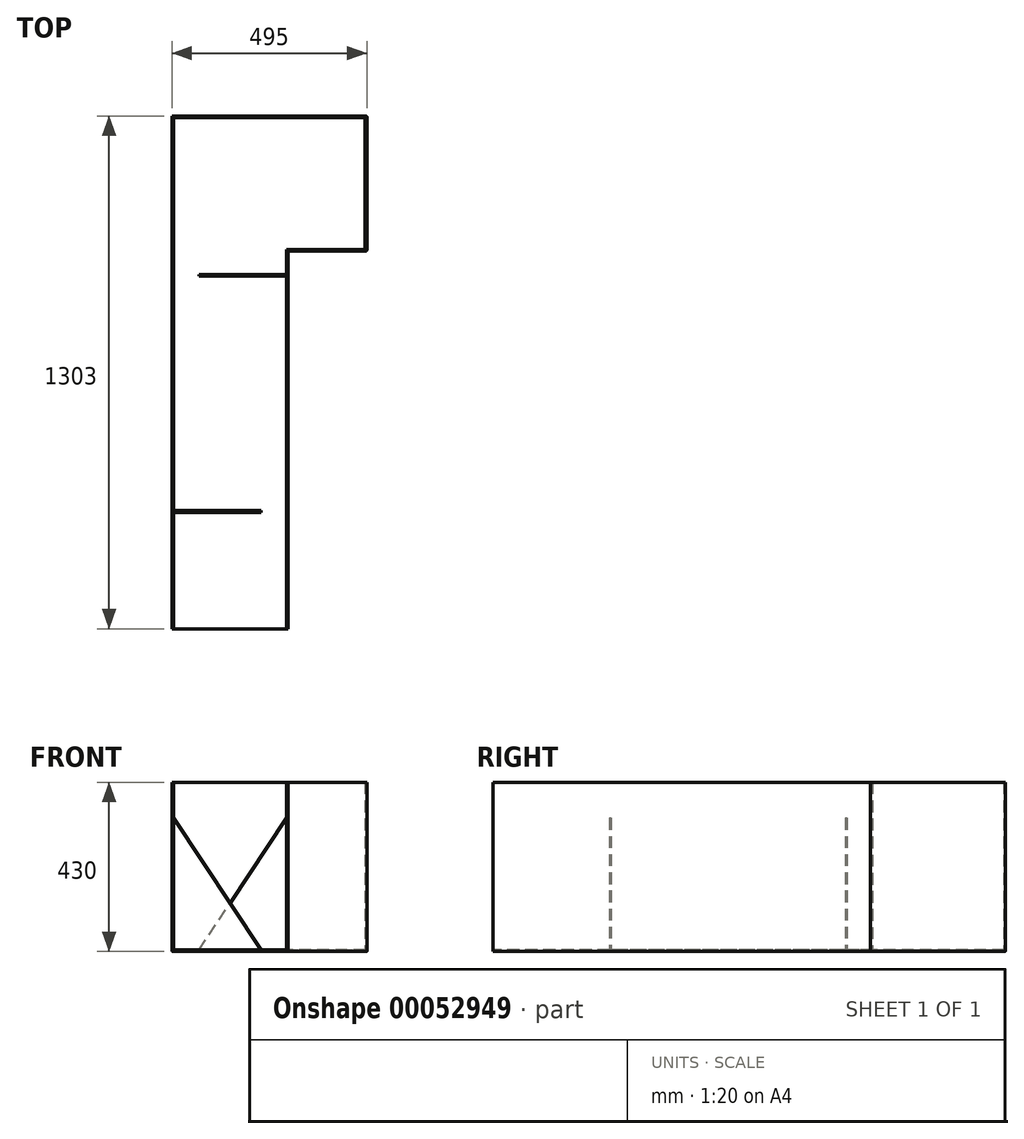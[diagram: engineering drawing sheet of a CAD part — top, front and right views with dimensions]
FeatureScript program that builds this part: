
annotation { "Feature Type Name" : "Feature", "Feature Type Description" : "" }
export const myFeature = defineFeature(function(context is Context, id is Id, definition is map)
    precondition{}
    {
        {
            var Q0;
            Q0=qCreatedBy(makeId("Top.planeOp"),FACE);
            var sketch = newSketch(context, id + "F0", { "sketchPlane" : qUnion([Q0])});
            skLineSegment(sketch, "E0", {"start": v(0, -343) * mm, "end": v(0, 0) * mm});
            skLineSegment(sketch, "E1.MirrorCS", {"start": v(-4, -339) * mm, "end": v(-4, -4) * mm});
            skLineSegment(sketch, "E2.MirrorCS", {"start": v(-4, -4) * mm, "end": v(-491, -4) * mm});
            skLineSegment(sketch, "E3.MirrorCS", {"start": v(0, 0) * mm, "end": v(-495, 0) * mm});
            skLineSegment(sketch, "E4.MirrorCS", {"start": v(-495, 0) * mm, "end": v(-495, -1303) * mm});
            skLineSegment(sketch, "E5.MirrorCS", {"start": v(-491, -4) * mm, "end": v(-491, -1303) * mm});
            skLineSegment(sketch, "E6.MirrorCS", {"start": v(-204, -339) * mm, "end": v(-204, -1303) * mm});
            skLineSegment(sketch, "E7.MirrorCS", {"start": v(-200, -343) * mm, "end": v(-200, -1303) * mm});
            skLineSegment(sketch, "E8.MirrorCS", {"start": v(-200, -343) * mm, "end": v(0, -343) * mm});
            skLineSegment(sketch, "E9.MirrorCS", {"start": v(-204, -339) * mm, "end": v(-4, -339) * mm});
            skLineSegment(sketch, "E10.MirrorCS", {"start": v(-204, -1303) * mm, "end": v(-200, -1303) * mm});
            skLineSegment(sketch, "E11.MirrorCS", {"start": v(-491, -1303) * mm, "end": v(-495, -1303) * mm});
            skSolve(sketch);
        }
        {
            var Q0;
            Q0=makeQuery(id+"F0.imprint","IMPRINT",FACE,{"disambiguationData":[TD([[makeQuery(id+"F0.imprint","IMPRINT",EDGE,{"derivedFrom":sQuery(id+"F0.wireOp",EDGE,"8549452f-c1c4-4c66-b43a-6f4cb653c117")}),-1.0]])]});
            var Q1;
            Q1=makeQuery(id+"F0.imprint","IMPRINT",FACE,{"disambiguationData":[TD([[makeQuery(id+"F0.imprint","IMPRINT",EDGE,{"derivedFrom":sQuery(id+"F0.wireOp",EDGE,"E0")}),1.0]])]});
            extrude(context, id + "F1", {"entities" : qUnion([Q0, Q1]), "depth" : 426 * mm});
        }
        {
            var Q0;
            Q0=qCreatedBy(makeId("Top.planeOp"),FACE);
            var sketch = newSketch(context, id + "F2", { "sketchPlane" : qUnion([Q0])});
            skLineSegment(sketch, "E12.0", {"start": v(-495, 0) * mm, "end": v(-495, -1303) * mm});
            skLineSegment(sketch, "E13.0", {"start": v(-200, -343) * mm, "end": v(-200, -1303) * mm});
            skLineSegment(sketch, "E14.0", {"start": v(-200, -343) * mm, "end": v(0, -343) * mm});
            skLineSegment(sketch, "E15.0", {"start": v(0, -343) * mm, "end": v(0, 0) * mm});
            skLineSegment(sketch, "E16.0", {"start": v(0, 0) * mm, "end": v(-495, 0) * mm});
            skLineSegment(sketch, "E17", {"start": v(-495, -1303) * mm, "end": v(-200, -1303) * mm});
            skSolve(sketch);
        }
        {
            var Q0;
            Q0=qSketchRegion(id+"F2",true);
            extrude(context, id + "F3", {"entities" : qUnion([Q0]), "operationType" : NewBodyOperationType.ADD, "oppositeDirection" : true, "depth" : 4 * mm});
        }
        {
            var Q0;
            Q0=makeQuery(id+"F3.opExtrude","CAP_EDGE",EDGE,{"disambiguationData":[OSD([sQuery(id+"F2.wireOp",EDGE,"e938920c-2318-497f-93e0-1fca7233731b.0")])],"isStart":false});
            var Q1;
            Q1=makeQuery(id+"F3.opExtrude","CAP_EDGE",EDGE,{"disambiguationData":[OSD([sQuery(id+"F2.wireOp",EDGE,"532a1349-e9fd-433e-8e1a-d463d1cb9540.0")])],"isStart":false});
            var Q2;
            Q2=makeQuery(id+"F3.opExtrude","CAP_EDGE",EDGE,{"disambiguationData":[OSD([sQuery(id+"F2.wireOp",EDGE,"f0b50a9b-8d41-4045-a57e-6e178546da08.0")])],"isStart":false});
            var Q3;
            Q3=makeQuery(id+"F3.opExtrude","CAP_EDGE",EDGE,{"disambiguationData":[OSD([sQuery(id+"F2.wireOp",EDGE,"76214740-f755-4499-b80f-307931e5da37.0")])],"isStart":false});
            var Q4;
            Q4=makeQuery(id+"F3.opExtrude","CAP_EDGE",EDGE,{"disambiguationData":[OSD([sQuery(id+"F2.wireOp",EDGE,"6fd2c64b-65cd-4597-b900-bc871f9f6c80.0")])],"isStart":false});
            var Q5;
            Q5=makeQuery(id+"F3.boolean.opBoolean","MERGE",EDGE,{"derivedFrom":[makeQuery(id+"F1.opExtrude","SWEPT_EDGE",EDGE,{"disambiguationData":[OSD([sQuery(id+"F0.wireOp",EDGE,"602087cb-8138-4325-86e3-c2d552e206f1"),sQuery(id+"F0.wireOp",EDGE,"5e85e9da-74ab-4066-82e7-4eeec8f45a40.right")])]}),makeQuery(id+"F3.opExtrude","SWEPT_EDGE",EDGE,{"disambiguationData":[OSD([sQuery(id+"F2.wireOp",EDGE,"532a1349-e9fd-433e-8e1a-d463d1cb9540.0"),sQuery(id+"F2.wireOp",EDGE,"f0b50a9b-8d41-4045-a57e-6e178546da08.0")])]})]});
            var Q6;
            Q6=makeQuery(id+"F3.boolean.opBoolean","MERGE",EDGE,{"derivedFrom":[makeQuery(id+"F1.opExtrude","SWEPT_EDGE",EDGE,{"disambiguationData":[OSD([sQuery(id+"F0.wireOp",EDGE,"602087cb-8138-4325-86e3-c2d552e206f1"),sQuery(id+"F0.wireOp",EDGE,"E0")])]}),makeQuery(id+"F3.opExtrude","SWEPT_EDGE",EDGE,{"disambiguationData":[OSD([sQuery(id+"F2.wireOp",EDGE,"532a1349-e9fd-433e-8e1a-d463d1cb9540.0"),sQuery(id+"F2.wireOp",EDGE,"76214740-f755-4499-b80f-307931e5da37.0")])]})]});
            var Q7;
            Q7=makeQuery(id+"F3.boolean.opBoolean","MERGE",EDGE,{"derivedFrom":[makeQuery(id+"F1.opExtrude","SWEPT_EDGE",EDGE,{"disambiguationData":[OSD([sQuery(id+"F0.wireOp",EDGE,"8549452f-c1c4-4c66-b43a-6f4cb653c117"),sQuery(id+"F0.wireOp",EDGE,"E0")])]}),makeQuery(id+"F3.opExtrude","SWEPT_EDGE",EDGE,{"disambiguationData":[OSD([sQuery(id+"F2.wireOp",EDGE,"76214740-f755-4499-b80f-307931e5da37.0"),sQuery(id+"F2.wireOp",EDGE,"6fd2c64b-65cd-4597-b900-bc871f9f6c80.0")])]})]});
            var Q8;
            Q8=makeQuery(id+"F1.opExtrude","SWEPT_EDGE",EDGE,{"disambiguationData":[OSD([sQuery(id+"F0.wireOp",EDGE,"41269a5a-69f6-4670-b1a7-19bf830e781a"),sQuery(id+"F0.wireOp",EDGE,"c0483dde-b345-4eca-95c5-d6ec0a503eff.right")])]});
            var Q9;
            Q9=makeQuery(id+"F1.opExtrude","SWEPT_EDGE",EDGE,{"disambiguationData":[OSD([sQuery(id+"F0.wireOp",EDGE,"cc5772d9-c29a-4c81-bde5-837d5d9decb7"),sQuery(id+"F0.wireOp",EDGE,"5e85e9da-74ab-4066-82e7-4eeec8f45a40.left")])]});
            var Q10;
            Q10=makeQuery(id+"F1.opExtrude","SWEPT_EDGE",EDGE,{"disambiguationData":[OSD([sQuery(id+"F0.wireOp",EDGE,"41269a5a-69f6-4670-b1a7-19bf830e781a"),sQuery(id+"F0.wireOp",EDGE,"05cfef9b-c223-4bdb-b400-77ea615546ad")])]});
            var Q11;
            Q11=makeQuery(id+"F1.opExtrude","SWEPT_EDGE",EDGE,{"disambiguationData":[OSD([sQuery(id+"F0.wireOp",EDGE,"05cfef9b-c223-4bdb-b400-77ea615546ad"),sQuery(id+"F0.wireOp",EDGE,"cc5772d9-c29a-4c81-bde5-837d5d9decb7")])]});
            var Q12;
            Q12=makeQuery(id+"F3.boolean.opBoolean","MERGE",EDGE,{"derivedFrom":[makeQuery(id+"F1.opExtrude","SWEPT_EDGE",EDGE,{"disambiguationData":[OSD([sQuery(id+"F0.wireOp",EDGE,"8549452f-c1c4-4c66-b43a-6f4cb653c117"),sQuery(id+"F0.wireOp",EDGE,"c0483dde-b345-4eca-95c5-d6ec0a503eff.left")])]}),makeQuery(id+"F3.opExtrude","SWEPT_EDGE",EDGE,{"disambiguationData":[OSD([sQuery(id+"F2.wireOp",EDGE,"6fd2c64b-65cd-4597-b900-bc871f9f6c80.0"),sQuery(id+"F2.wireOp",EDGE,"e938920c-2318-497f-93e0-1fca7233731b.0")])]})]});
            var Q13;
            Q13=makeQuery(id+"F3.opExtrude","CAP_EDGE",EDGE,{"disambiguationData":[OSD([sQuery(id+"F2.wireOp",EDGE,"E13.0")])],"isStart":false});
            var Q14;
            Q14=makeQuery(id+"F3.opExtrude","CAP_EDGE",EDGE,{"disambiguationData":[OSD([sQuery(id+"F2.wireOp",EDGE,"E12.0")])],"isStart":false});
            var Q15;
            Q15=makeQuery(id+"F3.opExtrude","CAP_EDGE",EDGE,{"disambiguationData":[OSD([sQuery(id+"F2.wireOp",EDGE,"E16.0")])],"isStart":false});
            fillet(context, id + "F4", {"entities" : qUnion([Q0, Q1, Q2, Q3, Q4, Q5, Q6, Q7, Q8, Q9, Q10, Q11, Q12, Q13, Q14, Q15]), "radius" : 2 * mm, "tangentPropagation" : true, "allowEdgeOverflow" : false});
        }
        {
            var Q0;
            Q0=makeQuery(id+"F3.boolean.opBoolean","MERGE",FACE,{"derivedFrom":[makeQuery(id+"F1.opExtrude","SWEPT_FACE",FACE,{"disambiguationData":[OSD([sQuery(id+"F0.wireOp",EDGE,"E10.MirrorCS")])]}),makeQuery(id+"F1.opExtrude","SWEPT_FACE",FACE,{"disambiguationData":[OSD([sQuery(id+"F0.wireOp",EDGE,"E11.MirrorCS")])]}),makeQuery(id+"F3.opExtrude","SWEPT_FACE",FACE,{"disambiguationData":[OSD([sQuery(id+"F2.wireOp",EDGE,"E17")])]})]});
            cPlane(context, id + "F5", {"entities" : qUnion([Q0]), "cplaneType" : CPlaneType.OFFSET, "offset" : 300 * mm, "oppositeDirection" : true, "width" : 150 * mm, "height" : 150 * mm});
        }
        {
            var Q0;
            Q0=qCreatedBy(id+"F5.planeOp",FACE);
            var sketch = newSketch(context, id + "F6", { "sketchPlane" : qUnion([Q0])});
            skLineSegment(sketch, "E18", {"start": v(-269, 0) * mm, "end": v(-491, 335) * mm});
            skLineSegment(sketch, "E19", {"start": v(-491, 335) * mm, "end": v(-491, 0) * mm});
            skLineSegment(sketch, "E20", {"start": v(-491, 0) * mm, "end": v(-269, 0) * mm});
            skSolve(sketch);
        }
        {
            var Q0;
            Q0 = qSketchRegion(id + "F6", true);
            extrude(context, id + "F7", {"entities" : qUnion([Q0]), "operationType" : NewBodyOperationType.ADD, "depth" : 4 * mm});
        }
        {
            var Q0;
            Q0=qCreatedBy(id+"F5.planeOp",FACE);
            cPlane(context, id + "F8", {"entities" : qUnion([Q0]), "cplaneType" : CPlaneType.OFFSET, "offset" : 600 * mm, "oppositeDirection" : true, "width" : 150 * mm, "height" : 150 * mm});
        }
        {
            var Q0;
            Q0=qCreatedBy(id+"F8.planeOp",FACE);
            var sketch = newSketch(context, id + "F9", { "sketchPlane" : qUnion([Q0])});
            skLineSegment(sketch, "E21", {"start": v(-426, 0) * mm, "end": v(-204, 335) * mm});
            skLineSegment(sketch, "E22", {"start": v(-204, 335) * mm, "end": v(-204, 0) * mm});
            skLineSegment(sketch, "E23", {"start": v(-204, 0) * mm, "end": v(-426, 0) * mm});
            skSolve(sketch);
        }
        {
            var Q0;
            Q0 = qSketchRegion(id + "F9", true);
            extrude(context, id + "F10", {"entities" : qUnion([Q0]), "operationType" : NewBodyOperationType.ADD, "depth" : 4 * mm});
        }
    });
